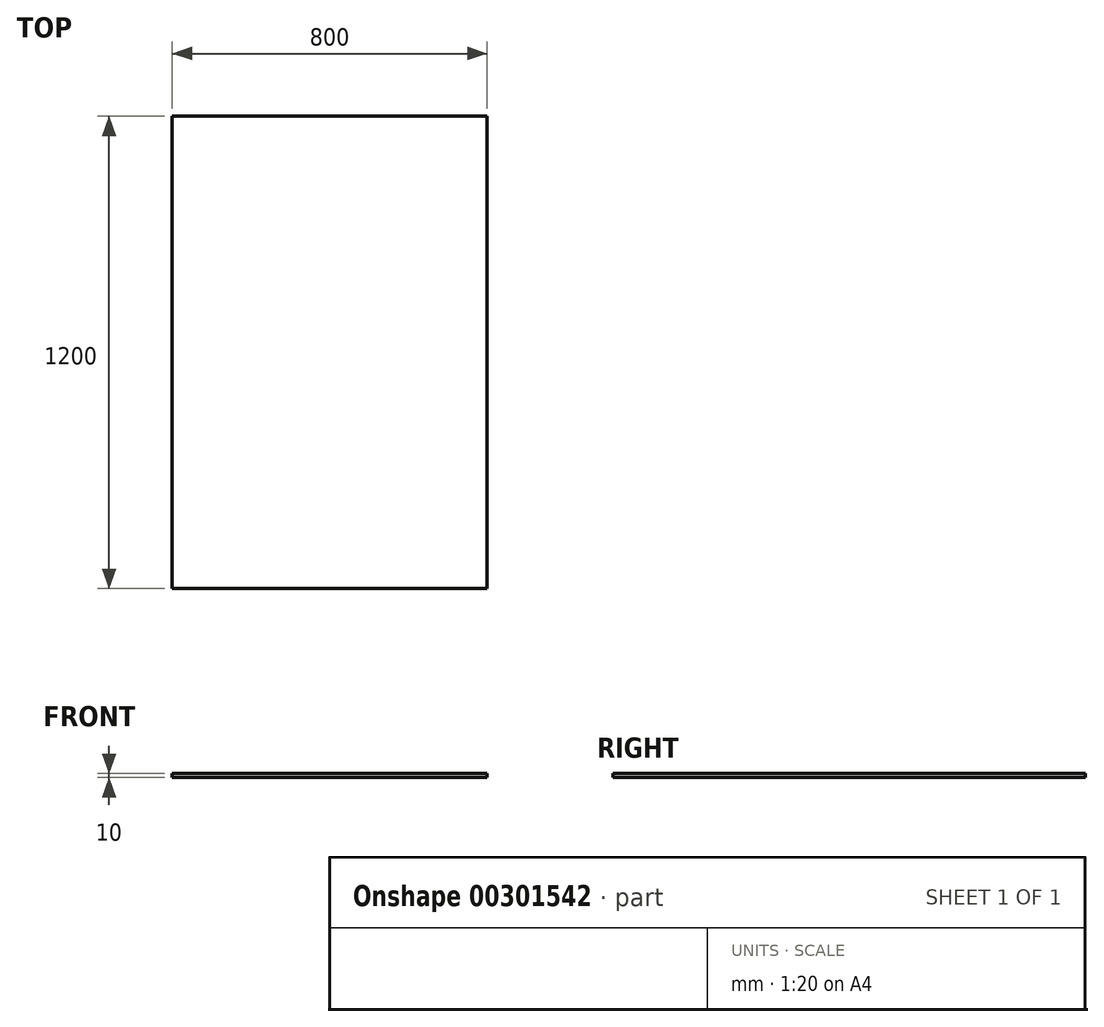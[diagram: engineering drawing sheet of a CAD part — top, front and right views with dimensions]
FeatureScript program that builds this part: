
annotation { "Feature Type Name" : "Feature", "Feature Type Description" : "" }
export const myFeature = defineFeature(function(context is Context, id is Id, definition is map)
    precondition{}
    {
        {
            var Q0;
            Q0=qCreatedBy(makeId("Top.planeOp"),FACE);
            var sketch = newSketch(context, id + "F0", { "sketchPlane" : qUnion([Q0])});
            skLineSegment(sketch, "E0.bottom", {"start": v(-400, 600) * mm, "end": v(400, 600) * mm});
            skLineSegment(sketch, "E0.top", {"start": v(-400, -600) * mm, "end": v(400, -600) * mm});
            skLineSegment(sketch, "E0.left", {"start": v(-400, 600) * mm, "end": v(-400, -600) * mm});
            skLineSegment(sketch, "E0.right", {"start": v(400, 600) * mm, "end": v(400, -600) * mm});
            skPoint(sketch, "E0.middle", {"position": v(0, 0) * mm});
            skSolve(sketch);
        }
        {
            var Q0;
            Q0 = qSketchRegion(id + "F0", true);
            extrude(context, id + "F1", {"entities" : qUnion([Q0]), "depth" : 10 * mm});
        }
    });
